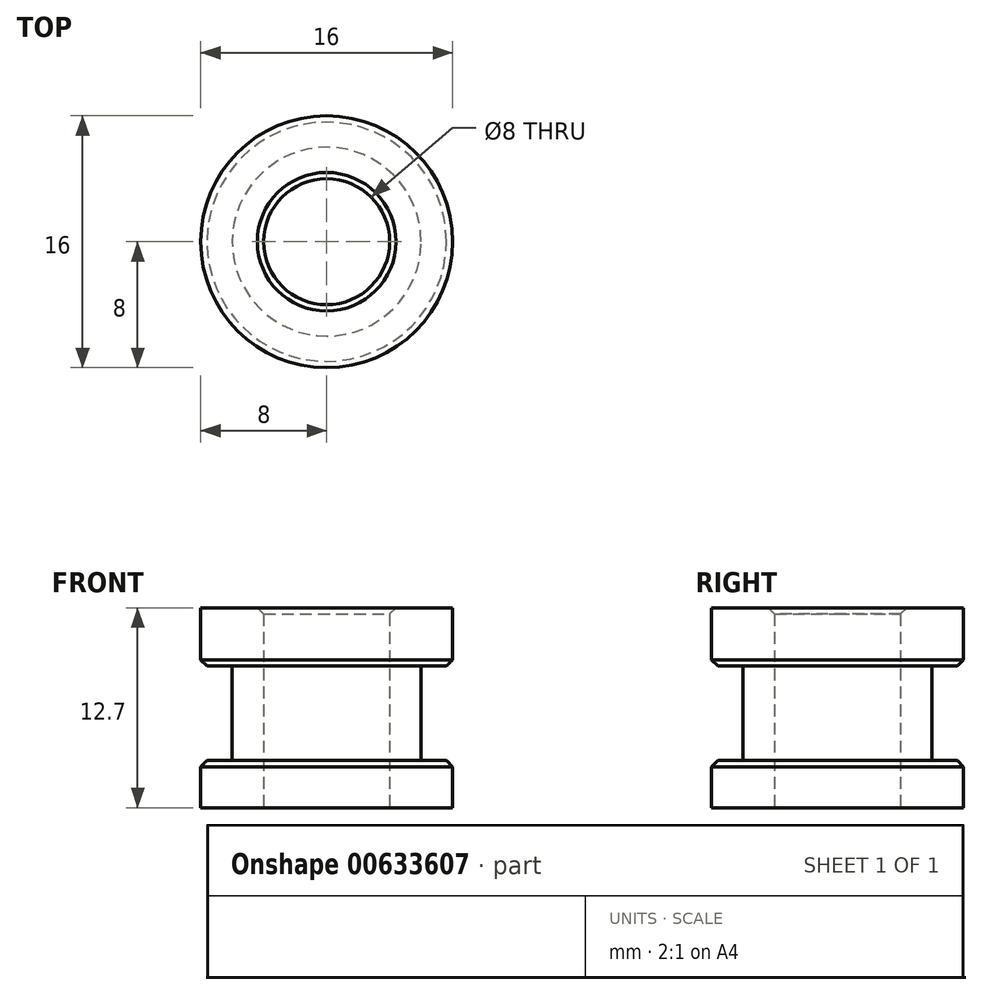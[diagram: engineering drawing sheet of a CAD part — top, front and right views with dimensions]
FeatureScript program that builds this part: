
annotation { "Feature Type Name" : "Feature", "Feature Type Description" : "" }
export const myFeature = defineFeature(function(context is Context, id is Id, definition is map)
    precondition{}
    {
        {
            var Q0;
            Q0=qCreatedBy(makeId("Front.planeOp"),FACE);
            var sketch = newSketch(context, id + "F0", { "sketchPlane" : qUnion([Q0])});
            skLineSegment(sketch, "E0", {"start": v(8, 6.7) * mm, "end": v(8, 3) * mm});
            skLineSegment(sketch, "E1", {"start": v(8, 3) * mm, "end": v(6, 3) * mm});
            skLineSegment(sketch, "E2", {"start": v(6, 3) * mm, "end": v(6, -3) * mm});
            skLineSegment(sketch, "E3", {"start": v(6, -3) * mm, "end": v(8, -3) * mm});
            skLineSegment(sketch, "E4", {"start": v(8, -3) * mm, "end": v(8, -6) * mm});
            skLineSegment(sketch, "E5", {"start": v(0, -5.39) * mm, "end": v(0, 5.39) * mm, "construction": true});
            skLineSegment(sketch, "E6", {"start": v(4, 6.7) * mm, "end": v(4, -6) * mm});
            skLineSegment(sketch, "E7", {"start": v(4, 6.7) * mm, "end": v(8, 6.7) * mm});
            skLineSegment(sketch, "E8", {"start": v(4, -6) * mm, "end": v(8, -6) * mm});
            skSolve(sketch);
        }
        {
            var Q0;
            Q0=qSketchRegion(id+"F0",true);
            var Q1;
            Q1=sQuery(id+"F0.wireOp",EDGE,"E5");
            revolve(context, id + "F1", {"entities" : qUnion([Q0]), "axis" : qUnion([Q1]), "revolveType" : RevolveType.FULL});
        }
        {
            var Q0;
            Q0=makeQuery(id+"F1.opRevolve","SWEPT_EDGE",EDGE,{"disambiguationData":[OSD([sQuery(id+"F0.wireOp",EDGE,"E0"),sQuery(id+"F0.wireOp",EDGE,"E1")])]});
            var Q1;
            Q1=makeQuery(id+"F1.opRevolve","SWEPT_EDGE",EDGE,{"disambiguationData":[OSD([sQuery(id+"F0.wireOp",EDGE,"E3"),sQuery(id+"F0.wireOp",EDGE,"E4")])]});
            var Q2;
            Q2=makeQuery(id+"F1.opRevolve","SWEPT_EDGE",EDGE,{"disambiguationData":[OSD([sQuery(id+"F0.wireOp",EDGE,"E6"),sQuery(id+"F0.wireOp",EDGE,"E7")])]});
            chamfer(context, id + "F2", {"entities" : qUnion([Q0, Q1, Q2]), "width" : 0.4 * mm, "tangentPropagation" : true});
        }
    });
